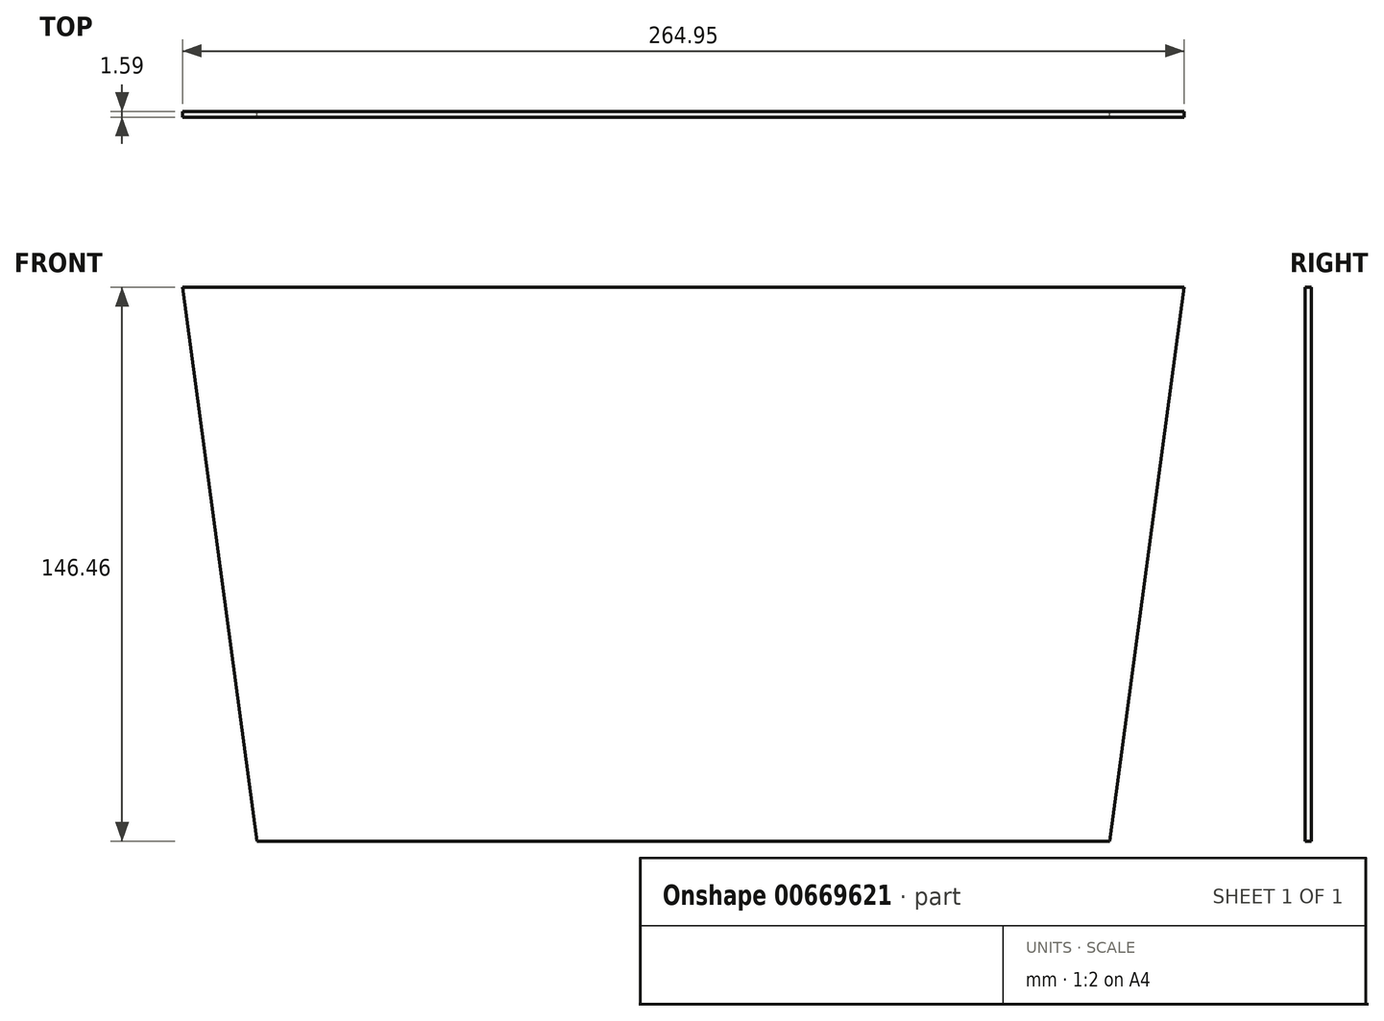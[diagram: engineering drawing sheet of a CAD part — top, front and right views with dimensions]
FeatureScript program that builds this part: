
annotation { "Feature Type Name" : "Feature", "Feature Type Description" : "" }
export const myFeature = defineFeature(function(context is Context, id is Id, definition is map)
    precondition{}
    {
        {
            var Q0;
            Q0=qCreatedBy(makeId("Front.planeOp"),FACE);
            var sketch = newSketch(context, id + "F0", { "sketchPlane" : qUnion([Q0])});
            skLineSegment(sketch, "E0", {"start": v(-158, 189.96) * mm, "end": v(106.94, 189.96) * mm});
            skLineSegment(sketch, "E1", {"start": v(106.94, 189.96) * mm, "end": v(87.23, 43.5) * mm});
            skLineSegment(sketch, "E2", {"start": v(87.23, 43.5) * mm, "end": v(-138.3, 43.5) * mm});
            skLineSegment(sketch, "E3", {"start": v(-138.3, 43.5) * mm, "end": v(-158, 189.96) * mm});
            skSolve(sketch);
        }
        {
            var Q0;
            Q0=qSketchRegion(id+"F0",true);
            extrude(context, id + "F1", {"entities" : qUnion([Q0]), "depth" : 1.59 * mm, "offsetDistance" : 25.4 * mm});
        }
    });
